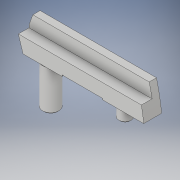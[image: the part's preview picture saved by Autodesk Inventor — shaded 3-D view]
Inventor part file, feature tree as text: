
AUTODESK INVENTOR PART (.ipt)
format: ipt  version: 2018.3 (Build 223284000, 284)  size: 182,272 bytes
history: native  units: in
note: dims shown in document units (in); Inventor stores cm internally (conversion verified against a paired STEP export)
features: sketch x4, extrude x2, revolve x2, plane x2
ambient origin geometry x8: Origin, YZ Plane, XZ Plane, XY Plane, X Axis, Y Axis, Z Axis, Center Point
bodies: Solid1 (feature_tree)
feature tree (10):
  sketch  "Sketch1"  dims[d0=0.02in d1=0.481in]
  extrude  "Extrusion1"  Depth=0.02in
  revolve  "Revolution1"  [1 undecoded]
  plane  "Work Plane1"
  extrude  "Extrusion2"  Depth=0.964in
  plane  "Work Plane2"
  revolve  "Revolution2"  [1 undecoded]
  sketch  "Sketch2"  dims[d3=3.626in d4=0.135in]
  sketch  "Sketch3"  dims[d5=0.22in d6=0.964in]
  sketch  "Sketch4"  dims[d7=0.312in d8=0.18in d9=0.784in d10=0.585in d11=0.01in d12=0.156in d13=0.1202in d14=0.138in d15=0.0in d16=0.0623in d17=0.32in d18=0.01in d19=45.0deg d20=90.0deg d21=0.012in d22=0.18in d23=-0.02in d24=0.138in d25=0.056in d26=0.138in d27=0.0in d28=0.013in d29=0.012in d30=0.765in d31=0.0483in d32=0.09in d33=0.01in d34=45.0deg d35=90.0deg]
note: 2 required parameter values undecoded (feature->parameter linkage not recoverable at this tier; creation-order binding heuristic only, values carry confidence <= 0.55)
